# Revit family: Toilet-Elongated_Contemporary_Neorest-600_MS990CGR_TOTO
name_source: partatom
category: Plumbing Fixtures
revit_build: Autodesk Revit Architecture 2013 (Build: 20130531_2115(x64)
units: mm (PartAtom-declared; Revit-internal decimal feet)

## types (1)
- MS990CGR
    04 CSI = 22 42 13
    95 CSI = 15410-800
    ADA Compliant = No
    Apparent Power = 1277 VA
    Assembly Code = D2010110
    Bowl Material = Vitreous China
    CAD Drawing URL = http://assets.totousa.com
    CW Connection = Yes
    CWFU = 0
    Certifications = IAPMO (cUPC), State of Massachusetts, City of Los Angeles, and others
    Code Compliance = UPC, IPC, NSPC, NPC Canada, and others
    Cold Water Connection NPT Radius = 0' - 0 1/4"
    Color Availability = #01 Cotton, #03 Bone, #12 Sedona Beige
    Default Elevation = 0' - 0"
    Description = Neorest® 600 Toilet, 1.6 GPF
    Finish = Vitreous China - TOTO - 01 Cotton
    Flush System = Cyclone Siphon Jet
    Frequency = 60 Hz
    Gallons Per Flush = 1.6 gal
    HW Connection = No
    HWFU = 0
    Height = 1' - 10 1/4"
    Industry Standards = Meets and exceeds ASME A112.19.2/CSA B45.1
    Length = 2' - 8 7/8"
    Manufacturer = TOTO USA, Inc.
    Manufacturer Fax = (770) 282-0002
    Model = MS990CGR
    Mount Type = Floor-Mounted
    Number of Poles = 1
    Rough in Availability = 12”
    Rough in Distance = 1' - 0"
    SanoGloss Available = Yes
    Seat Finish = Plastic - TOTO - 01 Cotton
    Seat Material = Plastic
    Series = Neorest
    Shipping Weight = 120.00 lb
    Spec Sheet URL = http://assets.totousa.com
    Style = Contemporary
    Subcategory = Toilets
    Toto BIM Number = BM-00019
    URL = http://www.totousa.com
    Vent Connection = Yes
    Voltage = 120 V
    WFU = 0
    Warranty = Three year Limited (Residential), One Year Limited (Commercial)
    Warranty URL = http://www.totousa.com
    Waste Connection = Yes
    Waste Connection NPT Radius = 0' - 1 7/32"
    WaterSense = No
    Width = 1' - 5 5/32"
    ecoScorecard Product Page = http://toto.ecoscorecard.com
    ecoScorecard_data = http://toto.ecoscorecard.com

## geometry (parser evidence)
native form markers: Blend x16, Sweep x1
no freeform markers — native parametric forms only
